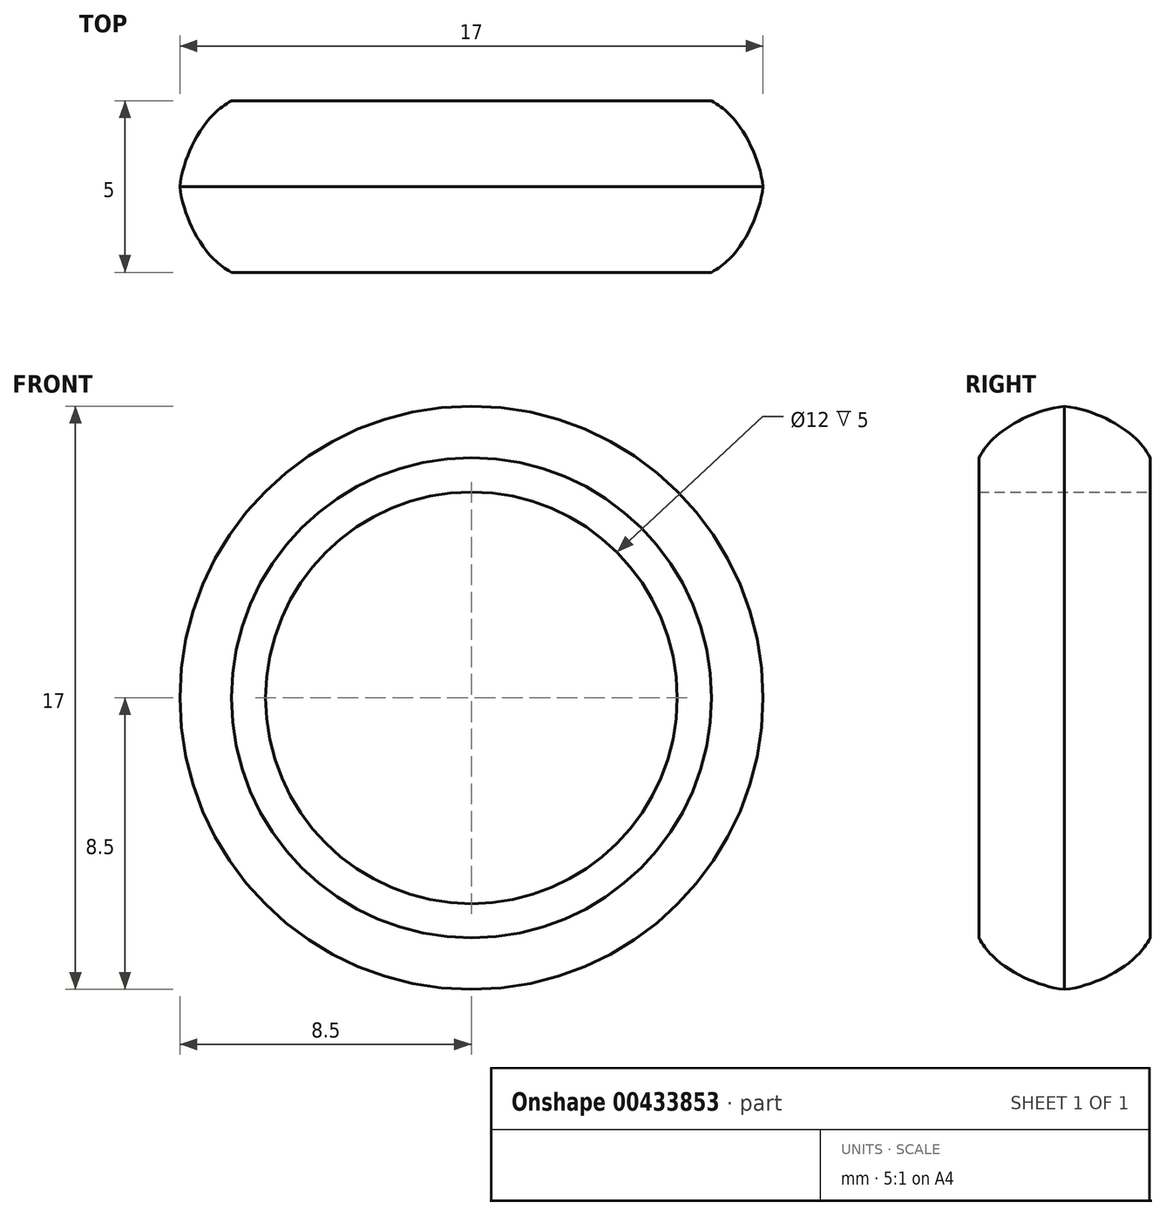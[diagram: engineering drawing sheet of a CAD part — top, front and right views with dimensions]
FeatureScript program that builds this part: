
annotation { "Feature Type Name" : "Feature", "Feature Type Description" : "" }
export const myFeature = defineFeature(function(context is Context, id is Id, definition is map)
    precondition{}
    {
        {
            var Q0;
            Q0=qCreatedBy(makeId("Front.planeOp"),FACE);
            var sketch = newSketch(context, id + "F0", { "sketchPlane" : qUnion([Q0])});
            skCircle(sketch, "E0", {"center": v(0, 0) * mm, "radius": 6 * mm});
            skSolve(sketch);
        }
        {
            var Q0;
            Q0=qCreatedBy(makeId("Right.planeOp"),FACE);
            var sketch = newSketch(context, id + "F1", { "sketchPlane" : qUnion([Q0])});
            skLineSegment(sketch, "E1", {"start": v(0, 6) * mm, "end": v(2.5, 6) * mm});
            skLineSegment(sketch, "E2", {"start": v(2.5, 6) * mm, "end": v(2.5, 7) * mm});
            skFitSpline(sketch, "E3", {"points": [v(2.5, 7) * mm, v(1.86, 7.74) * mm, v(0, 8.5) * mm], "startDerivative": vector(-1.18, 1.99) * mm, "endDerivative": vector(-3.68, 0.4) * mm});
            skFitSpline(sketch, "E4.MirrorCS", {"points": [v(-2.5, 7) * mm, v(-1.86, 7.74) * mm, v(0, 8.5) * mm], "startDerivative": vector(1.18, 1.99) * mm, "endDerivative": vector(3.68, 0.4) * mm});
            skLineSegment(sketch, "E5.MirrorCS", {"start": v(0, 6) * mm, "end": v(-2.5, 6) * mm});
            skLineSegment(sketch, "E6.MirrorCS", {"start": v(-2.5, 6) * mm, "end": v(-2.5, 7) * mm});
            skSolve(sketch);
        }
        {
            var Q0;
            Q0=makeQuery(id+"F1.imprint","IMPRINT",FACE,{"disambiguationData":[TD([[makeQuery(id+"F1.imprint","IMPRINT",EDGE,{"derivedFrom":sQuery(id+"F1.wireOp",EDGE,"E1")}),1.0]])]});
            var Q1;
            Q1=sQuery(id+"F0.wireOp",EDGE,"E0");
            revolve(context, id + "F2", {"entities" : qUnion([Q0]), "axis" : qUnion([Q1]), "revolveType" : RevolveType.FULL});
        }
    });
